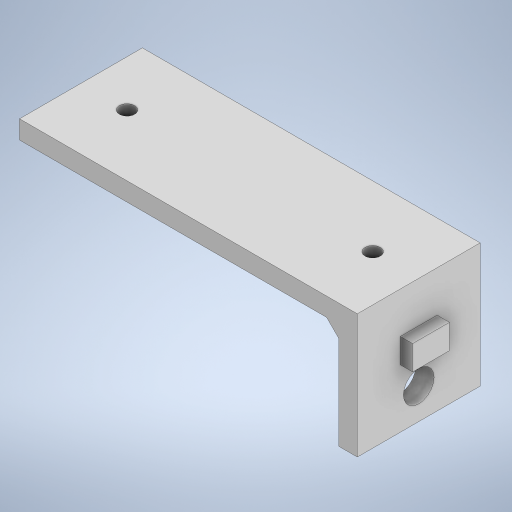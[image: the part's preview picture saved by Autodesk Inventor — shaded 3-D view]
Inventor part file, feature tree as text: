
AUTODESK INVENTOR PART (.ipt)
format: ipt  version: 2024 (Build 280153000, 153)  size: 256,512 bytes
history: native  units: mm
features: extrude x4, sketch x3, other x1, chamfer x1, projected_geometry x1
ambient origin geometry x8: Origin, YZ Plane, XZ Plane, XY Plane, X Axis, Y Axis, Z Axis, Center Point
bodies: Body1 (feature_tree)
feature tree (10):
  other  "솔리드1"
  sketch  "스케치1"
  extrude  "돌출1"  Depth=55.0mm
  extrude  "돌출2"  Depth=20.0mm
  sketch  "스케치2"
  chamfer  "모따기1"  Distance=3.0mm
  extrude  "돌출3"  Depth=3.0mm
  extrude  "돌출5"  Depth=17.2mm TaperAngle=0.0deg
  projected_geometry  "투영된 루프1"
  sketch  "스케치5"
